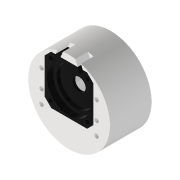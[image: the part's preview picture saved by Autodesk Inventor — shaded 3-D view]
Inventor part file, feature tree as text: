
AUTODESK INVENTOR PART (.ipt)
format: ipt  version: 2022 (Build 260153000, 153)  size: 446,464 bytes
history: native  units: mm
features: reference x22, sketch x6, extrude x5, other x4, projected_geometry x3, plane x1, hole x1
ambient origin geometry x8: Origin, YZ Plane, XZ Plane, XY Plane, X Axis, Y Axis, Z Axis, Center Point
bodies: Volumenkörper1 (feature_tree)
feature tree (42):
  extrude  "Extrusion1"  Depth=2.8mm
  sketch  "Skizze3"  dims[d2=8.0mm d3=0.0mm d4=0.5mm]
  plane  "Arbeitsebene1"
  extrude  "Extrusion2"  Depth=0.5mm
  extrude  "Extrusion3"  Depth=0.5mm
  hole  "Bohrung1"  [1 undecoded]
  extrude  "Extrusion4"  Depth=1.0mm TaperAngle=0.0deg
  extrude  "Extrusion5"  Depth=1.0mm
  sketch  "Skizze1"  dims[d0=2.8mm d1=2.8mm]
  reference  "Referenz1"
  reference  "Referenz2"
  reference  "Referenz3"
  reference  "Referenz4"
  reference  "Referenz5"
  reference  "Referenz7"
  reference  "Referenz8"
  reference  "Referenz9"
  reference  "Referenz10"
  reference  "Referenz11"
  reference  "Referenz12"
  reference  "Referenz13"
  reference  "Referenz14"
  reference  "Referenz15"
  reference  "Referenz16"
  reference  "Referenz17"
  reference  "Referenz18"
  reference  "Referenz19"
  sketch  "Skizze4"  dims[d5=0.5mm d6=0.5mm]
  projected_geometry  "Projizierte Kontur3"
  sketch  "Skizze5"  dims[d7=0.5mm d8=8.0mm d9=0.0mm]
  reference  "Referenz20"
  sketch  "Skizze6"  dims[d10=10.0mm d11=0.0mm]
  projected_geometry  "Projizierte Kontur4"
  sketch  "Skizze7"  dims[d12=2.8mm d13=6.0mm d14=6.5mm d15=23.0mm d16=90.0deg d17=15.0mm d18=20.594885mm d19=18.5mm d20=0.0mm d21=0.5mm d22=0.5mm d23=1.0mm d24=0.0mm]
  reference  "Referenz21"
  reference  "Referenz22"
  reference  "Referenz23"
  projected_geometry  "Projizierte Kontur5"
  other  "MeshFeature1"
  other  "Planktoscope_Mini_Peristalticpump.iam"
  other  "00_Stepper_Motor_28BYJ-48:1"
  other  "Matchboxscope_bottom_v0:1"
note: 1 required parameter value undecoded (feature->parameter linkage not recoverable at this tier; creation-order binding heuristic only, values carry confidence <= 0.55)
